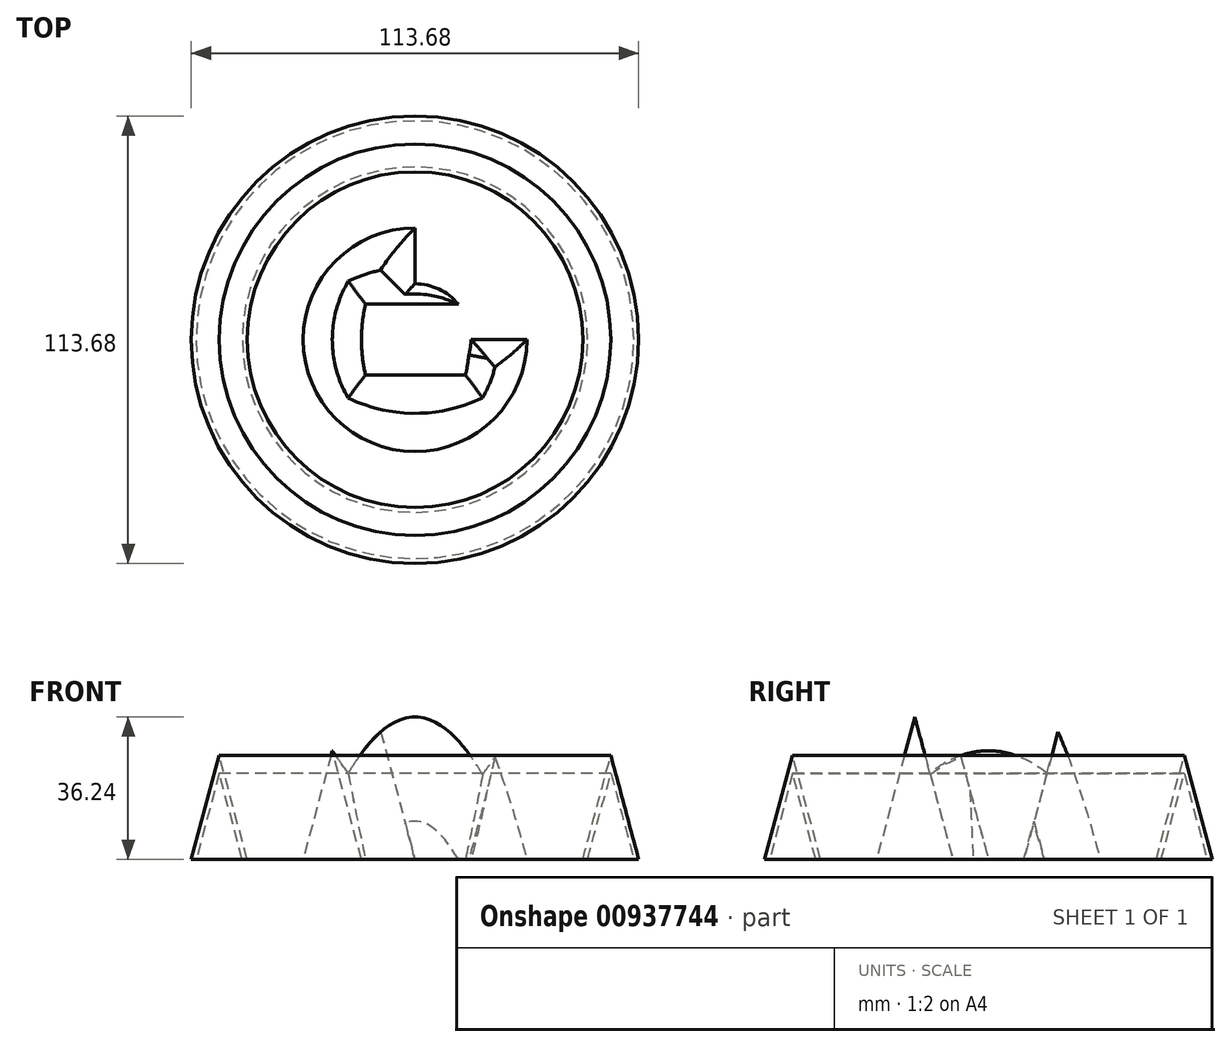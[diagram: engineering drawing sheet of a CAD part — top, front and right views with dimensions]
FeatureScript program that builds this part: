
annotation { "Feature Type Name" : "Feature", "Feature Type Description" : "" }
export const myFeature = defineFeature(function(context is Context, id is Id, definition is map)
    precondition{}
    {
        {
            var Q0;
            Q0=qCreatedBy(makeId("Top.planeOp"),FACE);
            var sketch = newSketch(context, id + "F0", { "sketchPlane" : qUnion([Q0])});
            skLineSegment(sketch, "E0", {"start": v(-28.42, 0) * mm, "end": v(-13.61, 0) * mm});
            skLineSegment(sketch, "E1", {"start": v(-56.84, 0) * mm, "end": v(-28.42, 0) * mm});
            skCircle(sketch, "E2", {"center": v(0, 0) * mm, "radius": 56.84 * mm});
            skCircle(sketch, "E3", {"center": v(0, 0) * mm, "radius": 28.42 * mm});
            skArc(sketch, "E4", {"start": v(-13.61, 0) * mm, "mid": v(-13.35, -4.53) * mm, "end": v(-12.57, -9) * mm});
            skArc(sketch, "E5", {"start": v(-12.57, 9) * mm, "mid": v(-13.35, 4.53) * mm, "end": v(-13.61, 0) * mm});
            skLineSegment(sketch, "E6", {"start": v(12.82, -9) * mm, "end": v(-12.57, -9) * mm});
            skArc(sketch, "E7", {"start": v(12.82, -9) * mm, "mid": v(13.86, 0) * mm, "end": v(12.82, 9) * mm});
            skLineSegment(sketch, "E8", {"start": v(-12.57, 9) * mm, "end": v(12.82, 9) * mm});
            skLineSegment(sketch, "E9", {"start": v(-12.57, -9) * mm, "end": v(12.82, -9) * mm});
            skLineSegment(sketch, "E10", {"start": v(12.43, 9) * mm, "end": v(-12.57, 9) * mm});
            skLineSegment(sketch, "E11", {"start": v(-13.61, 0) * mm, "end": v(-56.84, 0) * mm});
            skArc(sketch, "E12", {"start": v(-14.21, 0) * mm, "mid": v(-13.98, -2.56) * mm, "end": v(-13.29, -5.04) * mm});
            skArc(sketch, "E13", {"start": v(-11, -9) * mm, "mid": v(0, -14.21) * mm, "end": v(11, -9) * mm});
            skArc(sketch, "E14", {"start": v(13.66, -3.9) * mm, "mid": v(14.21, 0) * mm, "end": v(13.66, 3.9) * mm});
            skArc(sketch, "E15", {"start": v(11, 9) * mm, "mid": v(0, 14.21) * mm, "end": v(-11, 9) * mm});
            skArc(sketch, "E16", {"start": v(-13.29, 5.04) * mm, "mid": v(-13.98, 2.56) * mm, "end": v(-14.21, 0) * mm});
            skLineSegment(sketch, "E17", {"start": v(0, -28.42) * mm, "end": v(0, -9) * mm});
            skLineSegment(sketch, "E18", {"start": v(27.95, 0) * mm, "end": v(13.39, 0) * mm});
            skLineSegment(sketch, "E19", {"start": v(0, 28.42) * mm, "end": v(0, 9) * mm});
            skLineSegment(sketch, "E20", {"start": v(0, -9) * mm, "end": v(0, -56.84) * mm});
            skLineSegment(sketch, "E21", {"start": v(13.86, 0) * mm, "end": v(56.84, 0) * mm});
            skLineSegment(sketch, "E22", {"start": v(0, 9) * mm, "end": v(0, 56.84) * mm});
            skCircle(sketch, "E23", {"center": v(0, 0) * mm, "radius": 42.63 * mm});
            skLineSegment(sketch, "E24", {"start": v(0, -56.84) * mm, "end": v(0, -28.42) * mm});
            skLineSegment(sketch, "E25", {"start": v(56.84, 0) * mm, "end": v(28.42, 0) * mm});
            skLineSegment(sketch, "E26", {"start": v(0, 56.84) * mm, "end": v(0, 28.42) * mm});
            skArc(sketch, "E27", {"start": v(-12.57, 9) * mm, "mid": v(-13.61, 0) * mm, "end": v(-12.57, -9) * mm});
            skLineSegment(sketch, "E28", {"start": v(12.82, 9) * mm, "end": v(-12.57, 9) * mm});
            skSolve(sketch);
        }
        {
            var Q0;
            {var subQ0=sQuery(id+"F0.wireOp",EDGE,"E24");var subQ5=sQuery(id+"F0.wireOp",EDGE,"E23");var subQ6=makeQuery(id+"F0.imprint","INTERSECT",VERTEX,{"derivedFrom":[subQ5,subQ0]});Q0=makeQuery(id+"F0.imprint","IMPRINT",FACE,{"disambiguationData":[TD([[makeQuery(id+"F0.imprint","IMPRINT",EDGE,{"disambiguationData":[TD([[subQ6,1.0]])],"derivedFrom":subQ5}),-1.0]])]});}
            var Q1;
            {var subQ0=sQuery(id+"F0.wireOp",EDGE,"E3");var subQ1=sQuery(id+"F0.wireOp",EDGE,"E11");var subQ2=makeQuery(id+"F0.imprint","INTERSECT",VERTEX,{"derivedFrom":[subQ1,subQ0]});Q1=makeQuery(id+"F0.imprint","IMPRINT",FACE,{"disambiguationData":[TD([[makeQuery(id+"F0.imprint","IMPRINT",EDGE,{"disambiguationData":[TD([[subQ2,-1.0]])],"derivedFrom":subQ1}),-1.0]])]});}
            var Q2;
            {var subQ0=sQuery(id+"F0.wireOp",EDGE,"E9");var subQ1=sQuery(id+"F0.wireOp",EDGE,"E13");var subQ2=makeQuery(id+"F0.imprint","INTERSECT",VERTEX,{"disambiguationData":[OD(0.0)],"derivedFrom":[subQ1,subQ0]});Q2=makeQuery(id+"F0.imprint","IMPRINT",FACE,{"disambiguationData":[TD([[makeQuery(id+"F0.imprint","IMPRINT",EDGE,{"disambiguationData":[TD([[subQ2,-1.0]])],"derivedFrom":subQ1}),1.0]])]});}
            var Q3;
            {var subQ0=sQuery(id+"F0.wireOp",EDGE,"E28");var subQ1=sQuery(id+"F0.wireOp",EDGE,"E15");var subQ2=makeQuery(id+"F0.imprint","INTERSECT",VERTEX,{"disambiguationData":[OD(0.0)],"derivedFrom":[subQ1,subQ0]});Q3=makeQuery(id+"F0.imprint","IMPRINT",FACE,{"disambiguationData":[TD([[makeQuery(id+"F0.imprint","IMPRINT",EDGE,{"disambiguationData":[TD([[subQ2,-1.0]])],"derivedFrom":subQ1}),1.0]])]});}
            var Q4;
            {var subQ0=sQuery(id+"F0.wireOp",EDGE,"E9");var subQ1=sQuery(id+"F0.wireOp",EDGE,"E13");var subQ2=makeQuery(id+"F0.imprint","INTERSECT",VERTEX,{"disambiguationData":[OD(1.0)],"derivedFrom":[subQ1,subQ0]});Q4=makeQuery(id+"F0.imprint","IMPRINT",FACE,{"disambiguationData":[TD([[makeQuery(id+"F0.imprint","IMPRINT",EDGE,{"disambiguationData":[TD([[subQ2,1.0]])],"derivedFrom":subQ1}),1.0]])]});}
            var Q5;
            {var subQ3=sQuery(id+"F0.wireOp",EDGE,"E27");var subQ5=sQuery(id+"F0.wireOp",EDGE,"E4");var subQ6=makeQuery(id+"F0.imprint","INTERSECT",VERTEX,{"derivedFrom":[subQ5,subQ3]});Q5=makeQuery(id+"F0.imprint","IMPRINT",FACE,{"disambiguationData":[TD([[makeQuery(id+"F0.imprint","IMPRINT",EDGE,{"disambiguationData":[TD([[subQ6,1.0]])],"derivedFrom":subQ5}),1.0]])]});}
            var Q6;
            {var subQ9=sQuery(id+"F0.wireOp",EDGE,"E28");var subQ10=sQuery(id+"F0.wireOp",EDGE,"E15");var subQ11=makeQuery(id+"F0.imprint","INTERSECT",VERTEX,{"disambiguationData":[OD(1.0)],"derivedFrom":[subQ10,subQ9]});Q6=makeQuery(id+"F0.imprint","IMPRINT",FACE,{"disambiguationData":[TD([[makeQuery(id+"F0.imprint","IMPRINT",EDGE,{"disambiguationData":[TD([[subQ11,1.0]])],"derivedFrom":subQ10}),-1.0]])]});}
            var Q7;
            {var subQ10=sQuery(id+"F0.wireOp",EDGE,"E9");var subQ11=sQuery(id+"F0.wireOp",EDGE,"E13");var subQ12=makeQuery(id+"F0.imprint","INTERSECT",VERTEX,{"disambiguationData":[OD(0.0)],"derivedFrom":[subQ11,subQ10]});Q7=makeQuery(id+"F0.imprint","IMPRINT",FACE,{"disambiguationData":[TD([[makeQuery(id+"F0.imprint","IMPRINT",EDGE,{"disambiguationData":[TD([[subQ12,-1.0]])],"derivedFrom":subQ11}),-1.0]])]});}
            var Q8;
            {var subQ3=sQuery(id+"F0.wireOp",EDGE,"E14");var subQ11=sQuery(id+"F0.wireOp",EDGE,"E7");var subQ12=makeQuery(id+"F0.imprint","INTERSECT",VERTEX,{"disambiguationData":[OD(1.0)],"derivedFrom":[subQ3,subQ11]});Q8=makeQuery(id+"F0.imprint","IMPRINT",FACE,{"disambiguationData":[TD([[makeQuery(id+"F0.imprint","IMPRINT",EDGE,{"disambiguationData":[TD([[subQ12,1.0]])],"derivedFrom":subQ3}),-1.0]])]});}
            var Q9;
            {var subQ3=sQuery(id+"F0.wireOp",EDGE,"E13");var subQ11=sQuery(id+"F0.wireOp",EDGE,"E9");var subQ12=makeQuery(id+"F0.imprint","INTERSECT",VERTEX,{"disambiguationData":[OD(1.0)],"derivedFrom":[subQ3,subQ11]});Q9=makeQuery(id+"F0.imprint","IMPRINT",FACE,{"disambiguationData":[TD([[makeQuery(id+"F0.imprint","IMPRINT",EDGE,{"disambiguationData":[TD([[subQ12,1.0]])],"derivedFrom":subQ3}),-1.0]])]});}
            var Q10;
            {var subQ0=sQuery(id+"F0.wireOp",EDGE,"E25");var subQ5=sQuery(id+"F0.wireOp",EDGE,"E23");var subQ6=makeQuery(id+"F0.imprint","INTERSECT",VERTEX,{"derivedFrom":[subQ5,subQ0]});Q10=makeQuery(id+"F0.imprint","IMPRINT",FACE,{"disambiguationData":[TD([[makeQuery(id+"F0.imprint","IMPRINT",EDGE,{"disambiguationData":[TD([[subQ6,1.0]])],"derivedFrom":subQ5}),-1.0]])]});}
            var Q11;
            {var subQ0=sQuery(id+"F0.wireOp",EDGE,"E28");var subQ1=sQuery(id+"F0.wireOp",EDGE,"E15");var subQ2=makeQuery(id+"F0.imprint","INTERSECT",VERTEX,{"disambiguationData":[OD(1.0)],"derivedFrom":[subQ1,subQ0]});Q11=makeQuery(id+"F0.imprint","IMPRINT",FACE,{"disambiguationData":[TD([[makeQuery(id+"F0.imprint","IMPRINT",EDGE,{"disambiguationData":[TD([[subQ2,1.0]])],"derivedFrom":subQ1}),1.0]])]});}
            var Q12;
            {var subQ0=sQuery(id+"F0.wireOp",EDGE,"E7");var subQ1=sQuery(id+"F0.wireOp",EDGE,"E14");var subQ2=makeQuery(id+"F0.imprint","INTERSECT",VERTEX,{"disambiguationData":[OD(1.0)],"derivedFrom":[subQ1,subQ0]});Q12=makeQuery(id+"F0.imprint","IMPRINT",FACE,{"disambiguationData":[TD([[makeQuery(id+"F0.imprint","IMPRINT",EDGE,{"disambiguationData":[TD([[subQ2,1.0]])],"derivedFrom":subQ1}),1.0]])]});}
            var Q13;
            {var subQ0=sQuery(id+"F0.wireOp",EDGE,"E27");var subQ3=sQuery(id+"F0.wireOp",EDGE,"E12");var subQ5=makeQuery(id+"F0.imprint","INTERSECT",VERTEX,{"derivedFrom":[subQ3,subQ0]});Q13=makeQuery(id+"F0.imprint","IMPRINT",FACE,{"disambiguationData":[TD([[makeQuery(id+"F0.imprint","IMPRINT",EDGE,{"disambiguationData":[TD([[subQ5,1.0]])],"derivedFrom":subQ3}),1.0]])]});}
            var Q14;
            {var subQ1=sQuery(id+"F0.wireOp",EDGE,"E5");var subQ3=sQuery(id+"F0.wireOp",EDGE,"E16");var subQ4=makeQuery(id+"F0.imprint","INTERSECT",VERTEX,{"derivedFrom":[subQ1,subQ3]});Q14=makeQuery(id+"F0.imprint","IMPRINT",FACE,{"disambiguationData":[TD([[makeQuery(id+"F0.imprint","IMPRINT",EDGE,{"disambiguationData":[TD([[subQ4,-1.0]])],"derivedFrom":subQ3}),-1.0]])]});}
            var Q15;
            {var subQ0=sQuery(id+"F0.wireOp",EDGE,"E27");var subQ3=sQuery(id+"F0.wireOp",EDGE,"E16");var subQ5=makeQuery(id+"F0.imprint","INTERSECT",VERTEX,{"derivedFrom":[subQ3,subQ0]});Q15=makeQuery(id+"F0.imprint","IMPRINT",FACE,{"disambiguationData":[TD([[makeQuery(id+"F0.imprint","IMPRINT",EDGE,{"disambiguationData":[TD([[subQ5,-1.0]])],"derivedFrom":subQ3}),1.0]])]});}
            var Q16;
            {var subQ0=sQuery(id+"F0.wireOp",EDGE,"E7");var subQ1=sQuery(id+"F0.wireOp",EDGE,"E14");var subQ2=makeQuery(id+"F0.imprint","INTERSECT",VERTEX,{"disambiguationData":[OD(0.0)],"derivedFrom":[subQ1,subQ0]});Q16=makeQuery(id+"F0.imprint","IMPRINT",FACE,{"disambiguationData":[TD([[makeQuery(id+"F0.imprint","IMPRINT",EDGE,{"disambiguationData":[TD([[subQ2,-1.0]])],"derivedFrom":subQ1}),1.0]])]});}
            var Q17;
            {var subQ1=sQuery(id+"F0.wireOp",EDGE,"E5");var subQ3=sQuery(id+"F0.wireOp",EDGE,"E16");var subQ4=makeQuery(id+"F0.imprint","INTERSECT",VERTEX,{"derivedFrom":[subQ1,subQ3]});Q17=makeQuery(id+"F0.imprint","IMPRINT",FACE,{"disambiguationData":[TD([[makeQuery(id+"F0.imprint","IMPRINT",EDGE,{"disambiguationData":[TD([[subQ4,-1.0]])],"derivedFrom":subQ3}),1.0]])]});}
            var Q18;
            {var subQ0=sQuery(id+"F0.wireOp",EDGE,"E27");var subQ1=sQuery(id+"F0.wireOp",EDGE,"E4");var subQ2=makeQuery(id+"F0.imprint","INTERSECT",VERTEX,{"derivedFrom":[subQ1,subQ0]});Q18=makeQuery(id+"F0.imprint","IMPRINT",FACE,{"disambiguationData":[TD([[makeQuery(id+"F0.imprint","IMPRINT",EDGE,{"disambiguationData":[TD([[subQ2,1.0]])],"derivedFrom":subQ1}),-1.0]])]});}
            var Q19;
            {var subQ1=sQuery(id+"F0.wireOp",EDGE,"E4");var subQ3=sQuery(id+"F0.wireOp",EDGE,"E12");var subQ4=makeQuery(id+"F0.imprint","INTERSECT",VERTEX,{"derivedFrom":[subQ1,subQ3]});Q19=makeQuery(id+"F0.imprint","IMPRINT",FACE,{"disambiguationData":[TD([[makeQuery(id+"F0.imprint","IMPRINT",EDGE,{"disambiguationData":[TD([[subQ4,1.0]])],"derivedFrom":subQ3}),1.0]])]});}
            var Q20;
            {var subQ0=sQuery(id+"F0.wireOp",EDGE,"E3");var subQ1=sQuery(id+"F0.wireOp",EDGE,"E11");var subQ2=makeQuery(id+"F0.imprint","INTERSECT",VERTEX,{"derivedFrom":[subQ1,subQ0]});Q20=makeQuery(id+"F0.imprint","IMPRINT",FACE,{"disambiguationData":[TD([[makeQuery(id+"F0.imprint","IMPRINT",EDGE,{"disambiguationData":[TD([[subQ2,-1.0]])],"derivedFrom":subQ1}),1.0]])]});}
            extrude(context, id + "F1", {"entities" : qUnion([Q0, Q1, Q2, Q3, Q4, Q5, Q6, Q7, Q8, Q9, Q10, Q11, Q12, Q13, Q14, Q15, Q16, Q17, Q18, Q19, Q20]), "depth" : 40 * mm, "offsetDistance" : 25 * mm, "hasDraft" : true, "draftAngle" : 15 * degree, "draftPullDirection" : true});
        }
        {
            var Q0;
            {var subQ3=sQuery(id+"F0.wireOp",EDGE,"E27");var subQ5=sQuery(id+"F0.wireOp",EDGE,"E4");var subQ6=makeQuery(id+"F0.imprint","INTERSECT",VERTEX,{"derivedFrom":[subQ5,subQ3]});Q0=makeQuery(id+"F0.imprint","IMPRINT",FACE,{"disambiguationData":[TD([[makeQuery(id+"F0.imprint","IMPRINT",EDGE,{"disambiguationData":[TD([[subQ6,1.0]])],"derivedFrom":subQ5}),1.0]])]});}
            extrude(context, id + "F2", {"entities" : qUnion([Q0]), "operationType" : NewBodyOperationType.REMOVE, "depth" : 40 * mm, "offsetDistance" : 25 * mm});
        }
        {
            var Q0;
            Q0=makeQuery(id+"F1.opExtrude","CAP_FACE",FACE,{"disambiguationData":[OSD([sQuery(id+"F0.wireOp",EDGE,"E23")])],"isStart":true});
            shell(context, id + "F3", {"entities" : qUnion([Q0]), "thickness" : 1.2 * mm});
        }
    });
